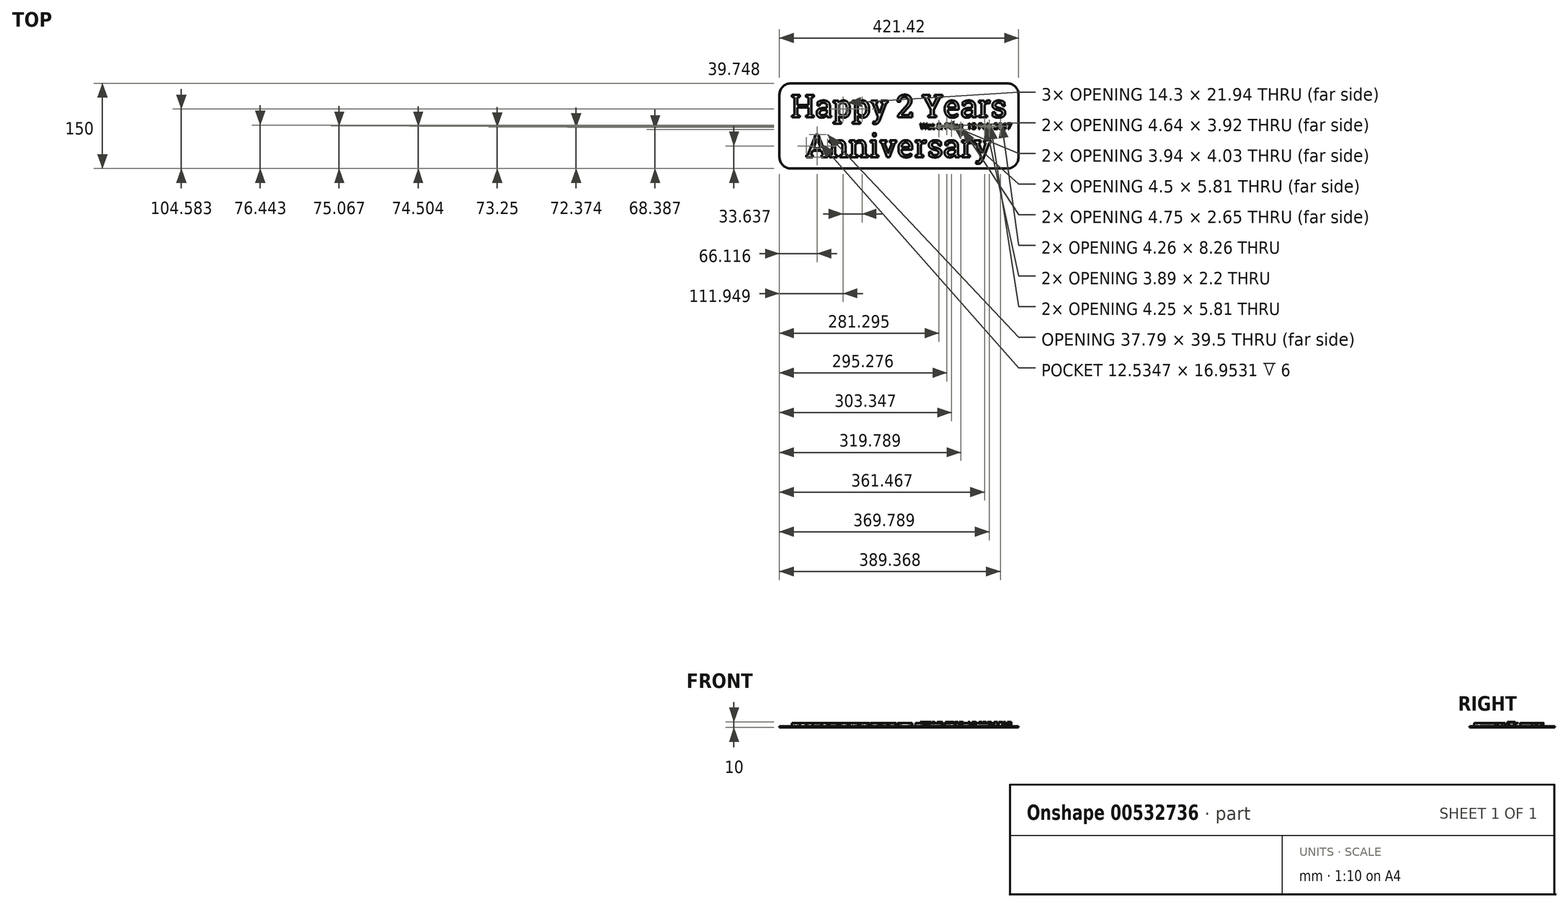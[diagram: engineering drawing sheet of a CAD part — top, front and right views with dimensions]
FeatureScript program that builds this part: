
annotation { "Feature Type Name" : "Feature", "Feature Type Description" : "" }
export const myFeature = defineFeature(function(context is Context, id is Id, definition is map)
    precondition{}
    {
        {
            var Q0;
            Q0=qCreatedBy(makeId("Top.planeOp"),FACE);
            var sketch = newSketch(context, id + "F0", { "sketchPlane" : qUnion([Q0])});
            skText(sketch, "E0", { "text": "Happy 2 Years\n", "fontName": "RobotoSlab-Regular.ttf"});
            skText(sketch, "E1", { "text": "Anniversary", "fontName": "RobotoSlab-Regular.ttf"});
            skLineSegment(sketch, "E2.bottom", {"start": v(-46.87, 27.18) * mm, "end": v(334.55, 27.18) * mm});
            skLineSegment(sketch, "E2.top", {"start": v(-46.87, -122.82) * mm, "end": v(334.55, -122.82) * mm});
            skLineSegment(sketch, "E2.left", {"start": v(-66.87, 7.18) * mm, "end": v(-66.87, -102.82) * mm});
            skLineSegment(sketch, "E2.right", {"start": v(354.55, 7.18) * mm, "end": v(354.55, -102.82) * mm});
            skPoint(sketch, "E3.visualSharp", {"position": v(354.55, 27.18) * mm});
            skArc(sketch, "E3.filletArc", {"start": v(354.55, 7.18) * mm, "mid": v(348.7, 21.32) * mm, "end": v(334.55, 27.18) * mm});
            skPoint(sketch, "E4.visualSharp", {"position": v(354.55, -122.82) * mm});
            skArc(sketch, "E4.filletArc", {"start": v(334.55, -122.82) * mm, "mid": v(348.7, -116.97) * mm, "end": v(354.55, -102.82) * mm});
            skPoint(sketch, "E5.visualSharp", {"position": v(-66.87, -122.82) * mm});
            skArc(sketch, "E5.filletArc", {"start": v(-66.87, -102.82) * mm, "mid": v(-61, -116.97) * mm, "end": v(-46.87, -122.82) * mm});
            skPoint(sketch, "E6.visualSharp", {"position": v(-66.87, 27.18) * mm});
            skArc(sketch, "E6.filletArc", {"start": v(-46.87, 27.18) * mm, "mid": v(-61, 21.32) * mm, "end": v(-66.87, 7.18) * mm});
            const initialGuessF0  = {"E0": [-0.04687, -0.03282, 1, 0, 0.04], "E1": [-0.02114, -0.10282, 1, 0, 0.04]};
            skSetInitialGuess(sketch, initialGuessF0);
            skSolve(sketch);
        }
        {
            var Q0;
            Q0=makeQuery(id+"F0.imprint","IMPRINT",FACE,{"disambiguationData":[TD([[makeQuery(id+"F0.imprint","IMPRINT",EDGE,{"derivedFrom":sQuery(id+"F0.wireOp",EDGE,"E0.sketch_text.stroke-0")}),1.0]])]});
            var sketch = newSketch(context, id + "F1", { "sketchPlane" : qUnion([Q0])});
            skText(sketch, "E7", { "text": "Wat & Pong  15 Feb 2017", "fontName": "OpenSans-Regular.ttf"});
            const initialGuessF1  = {"E7": [0.18108, -0.05328, 1, 0, 0.01]};
            skSetInitialGuess(sketch, initialGuessF1);
            skSolve(sketch);
        }
        {
            var Q0;
            Q0 = qSketchRegion(id + "F0", true);
            var Q1;
            Q1 = qSketchRegion(id + "F1", true);
            var Q2;
            Q2=makeQuery(id+"F0.imprint","IMPRINT",FACE,{"disambiguationData":[TD([[makeQuery(id+"F0.imprint","IMPRINT",EDGE,{"derivedFrom":sQuery(id+"F0.wireOp",EDGE,"E0.sketch_text.stroke-151")}),-1.0]])]});
            var Q3;
            Q3=makeQuery(id+"F0.imprint","IMPRINT",FACE,{"disambiguationData":[TD([[makeQuery(id+"F0.imprint","IMPRINT",EDGE,{"derivedFrom":sQuery(id+"F0.wireOp",EDGE,"E0.sketch_text.stroke-125")}),-1.0]])]});
            var Q4;
            Q4=makeQuery(id+"F0.imprint","IMPRINT",FACE,{"disambiguationData":[TD([[makeQuery(id+"F0.imprint","IMPRINT",EDGE,{"derivedFrom":sQuery(id+"F0.wireOp",EDGE,"E0.sketch_text.stroke-0")}),-1.0]])]});
            var Q5;
            Q5=makeQuery(id+"F0.imprint","IMPRINT",FACE,{"disambiguationData":[TD([[makeQuery(id+"F0.imprint","IMPRINT",EDGE,{"derivedFrom":sQuery(id+"F0.wireOp",EDGE,"E0.sketch_text.stroke-30")}),-1.0]])]});
            var Q6;
            Q6=makeQuery(id+"F0.imprint","IMPRINT",FACE,{"disambiguationData":[TD([[makeQuery(id+"F0.imprint","IMPRINT",EDGE,{"derivedFrom":sQuery(id+"F0.wireOp",EDGE,"E0.sketch_text.stroke-57")}),1.0]])]});
            var Q7;
            Q7=makeQuery(id+"F0.imprint","IMPRINT",FACE,{"disambiguationData":[TD([[makeQuery(id+"F0.imprint","IMPRINT",EDGE,{"derivedFrom":sQuery(id+"F0.wireOp",EDGE,"E0.sketch_text.stroke-65")}),-1.0]])]});
            var Q8;
            Q8=makeQuery(id+"F0.imprint","IMPRINT",FACE,{"disambiguationData":[TD([[makeQuery(id+"F0.imprint","IMPRINT",EDGE,{"derivedFrom":sQuery(id+"F0.wireOp",EDGE,"E0.sketch_text.stroke-85")}),1.0]])]});
            var Q9;
            Q9=makeQuery(id+"F0.imprint","IMPRINT",FACE,{"disambiguationData":[TD([[makeQuery(id+"F0.imprint","IMPRINT",EDGE,{"derivedFrom":sQuery(id+"F0.wireOp",EDGE,"E0.sketch_text.stroke-95")}),-1.0]])]});
            var Q10;
            Q10=makeQuery(id+"F1.imprint","IMPRINT",FACE,{"disambiguationData":[TD([[makeQuery(id+"F1.imprint","IMPRINT",EDGE,{"derivedFrom":makeQuery(id+"F0.imprint","IMPRINT",EDGE,{"derivedFrom":sQuery(id+"F0.wireOp",EDGE,"E0.sketch_text.stroke-95")})}),-1.0]])]});
            var Q11;
            Q11=makeQuery(id+"F0.imprint","IMPRINT",FACE,{"disambiguationData":[TD([[makeQuery(id+"F0.imprint","IMPRINT",EDGE,{"derivedFrom":sQuery(id+"F0.wireOp",EDGE,"E0.sketch_text.stroke-174")}),-1.0]])]});
            var Q12;
            Q12=makeQuery(id+"F0.imprint","IMPRINT",FACE,{"disambiguationData":[TD([[makeQuery(id+"F0.imprint","IMPRINT",EDGE,{"derivedFrom":sQuery(id+"F0.wireOp",EDGE,"E0.sketch_text.stroke-195")}),-1.0]])]});
            var Q13;
            Q13=makeQuery(id+"F0.imprint","IMPRINT",FACE,{"disambiguationData":[TD([[makeQuery(id+"F0.imprint","IMPRINT",EDGE,{"derivedFrom":sQuery(id+"F0.wireOp",EDGE,"E0.sketch_text.stroke-212")}),1.0]])]});
            var Q14;
            Q14=makeQuery(id+"F0.imprint","IMPRINT",FACE,{"disambiguationData":[TD([[makeQuery(id+"F0.imprint","IMPRINT",EDGE,{"derivedFrom":sQuery(id+"F0.wireOp",EDGE,"E0.sketch_text.stroke-246")}),1.0]])]});
            var Q15;
            Q15=makeQuery(id+"F0.imprint","IMPRINT",FACE,{"disambiguationData":[TD([[makeQuery(id+"F0.imprint","IMPRINT",EDGE,{"derivedFrom":sQuery(id+"F0.wireOp",EDGE,"E0.sketch_text.stroke-219")}),-1.0]])]});
            var Q16;
            Q16=makeQuery(id+"F0.imprint","IMPRINT",FACE,{"disambiguationData":[TD([[makeQuery(id+"F0.imprint","IMPRINT",EDGE,{"derivedFrom":sQuery(id+"F0.wireOp",EDGE,"E0.sketch_text.stroke-254")}),-1.0]])]});
            var Q17;
            Q17=makeQuery(id+"F0.imprint","IMPRINT",FACE,{"disambiguationData":[TD([[makeQuery(id+"F0.imprint","IMPRINT",EDGE,{"derivedFrom":sQuery(id+"F0.wireOp",EDGE,"E0.sketch_text.stroke-273")}),-1.0]])]});
            var Q18;
            Q18=makeQuery(id+"F0.imprint","IMPRINT",FACE,{"disambiguationData":[TD([[makeQuery(id+"F0.imprint","IMPRINT",EDGE,{"derivedFrom":sQuery(id+"F0.wireOp",EDGE,"E1.sketch_text.stroke-231")}),-1.0]])]});
            var Q19;
            Q19=makeQuery(id+"F0.imprint","IMPRINT",FACE,{"disambiguationData":[TD([[makeQuery(id+"F0.imprint","IMPRINT",EDGE,{"derivedFrom":sQuery(id+"F0.wireOp",EDGE,"E1.sketch_text.stroke-212")}),-1.0]])]});
            var Q20;
            Q20=makeQuery(id+"F0.imprint","IMPRINT",FACE,{"disambiguationData":[TD([[makeQuery(id+"F0.imprint","IMPRINT",EDGE,{"derivedFrom":sQuery(id+"F0.wireOp",EDGE,"E1.sketch_text.stroke-177")}),-1.0]])]});
            var Q21;
            Q21=makeQuery(id+"F0.imprint","IMPRINT",FACE,{"disambiguationData":[TD([[makeQuery(id+"F0.imprint","IMPRINT",EDGE,{"derivedFrom":sQuery(id+"F0.wireOp",EDGE,"E1.sketch_text.stroke-204")}),1.0]])]});
            var Q22;
            Q22=makeQuery(id+"F0.imprint","IMPRINT",FACE,{"disambiguationData":[TD([[makeQuery(id+"F0.imprint","IMPRINT",EDGE,{"derivedFrom":sQuery(id+"F0.wireOp",EDGE,"E1.sketch_text.stroke-147")}),-1.0]])]});
            var Q23;
            Q23=makeQuery(id+"F0.imprint","IMPRINT",FACE,{"disambiguationData":[TD([[makeQuery(id+"F0.imprint","IMPRINT",EDGE,{"derivedFrom":sQuery(id+"F0.wireOp",EDGE,"E1.sketch_text.stroke-128")}),-1.0]])]});
            var Q24;
            Q24=makeQuery(id+"F0.imprint","IMPRINT",FACE,{"disambiguationData":[TD([[makeQuery(id+"F0.imprint","IMPRINT",EDGE,{"derivedFrom":sQuery(id+"F0.wireOp",EDGE,"E1.sketch_text.stroke-86")}),-1.0]])]});
            var Q25;
            Q25=makeQuery(id+"F0.imprint","IMPRINT",FACE,{"disambiguationData":[TD([[makeQuery(id+"F0.imprint","IMPRINT",EDGE,{"derivedFrom":sQuery(id+"F0.wireOp",EDGE,"E1.sketch_text.stroke-72")}),-1.0]])]});
            var Q26;
            Q26=makeQuery(id+"F0.imprint","IMPRINT",FACE,{"disambiguationData":[TD([[makeQuery(id+"F0.imprint","IMPRINT",EDGE,{"derivedFrom":sQuery(id+"F0.wireOp",EDGE,"E1.sketch_text.stroke-82")}),-1.0]])]});
            var Q27;
            Q27=makeQuery(id+"F0.imprint","IMPRINT",FACE,{"disambiguationData":[TD([[makeQuery(id+"F0.imprint","IMPRINT",EDGE,{"derivedFrom":sQuery(id+"F0.wireOp",EDGE,"E1.sketch_text.stroke-46")}),-1.0]])]});
            var Q28;
            Q28=makeQuery(id+"F0.imprint","IMPRINT",FACE,{"disambiguationData":[TD([[makeQuery(id+"F0.imprint","IMPRINT",EDGE,{"derivedFrom":sQuery(id+"F0.wireOp",EDGE,"E1.sketch_text.stroke-104")}),-1.0]])]});
            var Q29;
            Q29=makeQuery(id+"F0.imprint","IMPRINT",FACE,{"disambiguationData":[TD([[makeQuery(id+"F0.imprint","IMPRINT",EDGE,{"derivedFrom":sQuery(id+"F0.wireOp",EDGE,"E1.sketch_text.stroke-121")}),1.0]])]});
            var Q30;
            Q30=makeQuery(id+"F0.imprint","IMPRINT",FACE,{"disambiguationData":[TD([[makeQuery(id+"F0.imprint","IMPRINT",EDGE,{"derivedFrom":sQuery(id+"F0.wireOp",EDGE,"E1.sketch_text.stroke-20")}),-1.0]])]});
            var Q31;
            Q31=makeQuery(id+"F1.imprint","IMPRINT",FACE,{"disambiguationData":[TD([[makeQuery(id+"F1.imprint","IMPRINT",EDGE,{"derivedFrom":makeQuery(id+"F0.imprint","IMPRINT",EDGE,{"derivedFrom":sQuery(id+"F0.wireOp",EDGE,"E1.sketch_text.stroke-0")})}),-1.0]])]});
            var Q32;
            Q32=makeQuery(id+"F0.imprint","IMPRINT",FACE,{"disambiguationData":[TD([[makeQuery(id+"F0.imprint","IMPRINT",EDGE,{"derivedFrom":sQuery(id+"F0.wireOp",EDGE,"E1.sketch_text.stroke-16")}),1.0]])]});
            extrude(context, id + "F2", {"entities" : qUnion([Q0, Q1, Q2, Q3, Q4, Q5, Q6, Q7, Q8, Q9, Q10, Q11, Q12, Q13, Q14, Q15, Q16, Q17, Q18, Q19, Q20, Q21, Q22, Q23, Q24, Q25, Q26, Q27, Q28, Q29, Q30, Q31, Q32]), "depth" : 2 * mm, "offsetDistance" : 25 * mm});
        }
        {
            var Q0;
            Q0=makeQuery(id+"F1.imprint","IMPRINT",FACE,{"disambiguationData":[TD([[makeQuery(id+"F1.imprint","IMPRINT",EDGE,{"derivedFrom":makeQuery(id+"F0.imprint","IMPRINT",EDGE,{"derivedFrom":sQuery(id+"F0.wireOp",EDGE,"E0.sketch_text.stroke-30")})}),-1.0]])]});
            var Q1;
            Q1=makeQuery(id+"F1.imprint","IMPRINT",FACE,{"disambiguationData":[TD([[makeQuery(id+"F1.imprint","IMPRINT",EDGE,{"derivedFrom":makeQuery(id+"F0.imprint","IMPRINT",EDGE,{"derivedFrom":sQuery(id+"F0.wireOp",EDGE,"E0.sketch_text.stroke-219")})}),-1.0]])]});
            var Q2;
            Q2=makeQuery(id+"F1.imprint","IMPRINT",FACE,{"disambiguationData":[TD([[makeQuery(id+"F1.imprint","IMPRINT",EDGE,{"derivedFrom":makeQuery(id+"F0.imprint","IMPRINT",EDGE,{"derivedFrom":sQuery(id+"F0.wireOp",EDGE,"E1.sketch_text.stroke-0")})}),-1.0]])]});
            var Q3;
            Q3=makeQuery(id+"F0.imprint","IMPRINT",FACE,{"disambiguationData":[TD([[makeQuery(id+"F0.imprint","IMPRINT",EDGE,{"derivedFrom":sQuery(id+"F0.wireOp",EDGE,"E1.sketch_text.stroke-72")}),-1.0]])]});
            var Q4;
            Q4=makeQuery(id+"F1.imprint","IMPRINT",FACE,{"disambiguationData":[TD([[makeQuery(id+"F1.imprint","IMPRINT",EDGE,{"derivedFrom":makeQuery(id+"F0.imprint","IMPRINT",EDGE,{"derivedFrom":sQuery(id+"F0.wireOp",EDGE,"E1.sketch_text.stroke-82")})}),-1.0]])]});
            var Q5;
            Q5=makeQuery(id+"F0.imprint","IMPRINT",FACE,{"disambiguationData":[TD([[makeQuery(id+"F0.imprint","IMPRINT",EDGE,{"derivedFrom":sQuery(id+"F0.wireOp",EDGE,"E1.sketch_text.stroke-86")}),-1.0]])]});
            var Q6;
            Q6=makeQuery(id+"F1.imprint","IMPRINT",FACE,{"disambiguationData":[TD([[makeQuery(id+"F1.imprint","IMPRINT",EDGE,{"derivedFrom":makeQuery(id+"F0.imprint","IMPRINT",EDGE,{"derivedFrom":sQuery(id+"F0.wireOp",EDGE,"E1.sketch_text.stroke-104")})}),-1.0]])]});
            var Q7;
            Q7=makeQuery(id+"F0.imprint","IMPRINT",FACE,{"disambiguationData":[TD([[makeQuery(id+"F0.imprint","IMPRINT",EDGE,{"derivedFrom":sQuery(id+"F0.wireOp",EDGE,"E1.sketch_text.stroke-128")}),-1.0]])]});
            var Q8;
            Q8=makeQuery(id+"F0.imprint","IMPRINT",FACE,{"disambiguationData":[TD([[makeQuery(id+"F0.imprint","IMPRINT",EDGE,{"derivedFrom":sQuery(id+"F0.wireOp",EDGE,"E1.sketch_text.stroke-147")}),-1.0]])]});
            var Q9;
            Q9=makeQuery(id+"F1.imprint","IMPRINT",FACE,{"disambiguationData":[TD([[makeQuery(id+"F1.imprint","IMPRINT",EDGE,{"derivedFrom":makeQuery(id+"F0.imprint","IMPRINT",EDGE,{"derivedFrom":sQuery(id+"F0.wireOp",EDGE,"E1.sketch_text.stroke-177")})}),-1.0]])]});
            var Q10;
            Q10=makeQuery(id+"F0.imprint","IMPRINT",FACE,{"disambiguationData":[TD([[makeQuery(id+"F0.imprint","IMPRINT",EDGE,{"derivedFrom":sQuery(id+"F0.wireOp",EDGE,"E1.sketch_text.stroke-20")}),-1.0]])]});
            var Q11;
            Q11=makeQuery(id+"F0.imprint","IMPRINT",FACE,{"disambiguationData":[TD([[makeQuery(id+"F0.imprint","IMPRINT",EDGE,{"derivedFrom":sQuery(id+"F0.wireOp",EDGE,"E1.sketch_text.stroke-46")}),-1.0]])]});
            var Q12;
            Q12=makeQuery(id+"F0.imprint","IMPRINT",FACE,{"disambiguationData":[TD([[makeQuery(id+"F0.imprint","IMPRINT",EDGE,{"derivedFrom":sQuery(id+"F0.wireOp",EDGE,"E1.sketch_text.stroke-212")}),-1.0]])]});
            var Q13;
            Q13=makeQuery(id+"F0.imprint","IMPRINT",FACE,{"disambiguationData":[TD([[makeQuery(id+"F0.imprint","IMPRINT",EDGE,{"derivedFrom":sQuery(id+"F0.wireOp",EDGE,"E1.sketch_text.stroke-231")}),-1.0]])]});
            var Q14;
            Q14=makeQuery(id+"F0.imprint","IMPRINT",FACE,{"disambiguationData":[TD([[makeQuery(id+"F0.imprint","IMPRINT",EDGE,{"derivedFrom":sQuery(id+"F0.wireOp",EDGE,"E0.sketch_text.stroke-0")}),-1.0]])]});
            var Q15;
            Q15=makeQuery(id+"F0.imprint","IMPRINT",FACE,{"disambiguationData":[TD([[makeQuery(id+"F0.imprint","IMPRINT",EDGE,{"derivedFrom":sQuery(id+"F0.wireOp",EDGE,"E0.sketch_text.stroke-65")}),-1.0]])]});
            var Q16;
            Q16=makeQuery(id+"F0.imprint","IMPRINT",FACE,{"disambiguationData":[TD([[makeQuery(id+"F0.imprint","IMPRINT",EDGE,{"derivedFrom":sQuery(id+"F0.wireOp",EDGE,"E0.sketch_text.stroke-95")}),-1.0]])]});
            var Q17;
            Q17=makeQuery(id+"F0.imprint","IMPRINT",FACE,{"disambiguationData":[TD([[makeQuery(id+"F0.imprint","IMPRINT",EDGE,{"derivedFrom":sQuery(id+"F0.wireOp",EDGE,"E0.sketch_text.stroke-125")}),-1.0]])]});
            var Q18;
            Q18=makeQuery(id+"F0.imprint","IMPRINT",FACE,{"disambiguationData":[TD([[makeQuery(id+"F0.imprint","IMPRINT",EDGE,{"derivedFrom":sQuery(id+"F0.wireOp",EDGE,"E0.sketch_text.stroke-151")}),-1.0]])]});
            var Q19;
            Q19=makeQuery(id+"F0.imprint","IMPRINT",FACE,{"disambiguationData":[TD([[makeQuery(id+"F0.imprint","IMPRINT",EDGE,{"derivedFrom":sQuery(id+"F0.wireOp",EDGE,"E0.sketch_text.stroke-174")}),-1.0]])]});
            var Q20;
            Q20=makeQuery(id+"F0.imprint","IMPRINT",FACE,{"disambiguationData":[TD([[makeQuery(id+"F0.imprint","IMPRINT",EDGE,{"derivedFrom":sQuery(id+"F0.wireOp",EDGE,"E0.sketch_text.stroke-195")}),-1.0]])]});
            var Q21;
            Q21=makeQuery(id+"F0.imprint","IMPRINT",FACE,{"disambiguationData":[TD([[makeQuery(id+"F0.imprint","IMPRINT",EDGE,{"derivedFrom":sQuery(id+"F0.wireOp",EDGE,"E1.sketch_text.stroke-16")}),1.0]])]});
            var Q22;
            Q22=makeQuery(id+"F0.imprint","IMPRINT",FACE,{"disambiguationData":[TD([[makeQuery(id+"F0.imprint","IMPRINT",EDGE,{"derivedFrom":sQuery(id+"F0.wireOp",EDGE,"E0.sketch_text.stroke-254")}),-1.0]])]});
            var Q23;
            Q23=makeQuery(id+"F0.imprint","IMPRINT",FACE,{"disambiguationData":[TD([[makeQuery(id+"F0.imprint","IMPRINT",EDGE,{"derivedFrom":sQuery(id+"F0.wireOp",EDGE,"E0.sketch_text.stroke-273")}),-1.0]])]});
            var Q24;
            Q24=makeQuery(id+"F0.imprint","IMPRINT",FACE,{"disambiguationData":[TD([[makeQuery(id+"F0.imprint","IMPRINT",EDGE,{"derivedFrom":sQuery(id+"F0.wireOp",EDGE,"E0.sketch_text.stroke-57")}),1.0]])]});
            var Q25;
            Q25=makeQuery(id+"F0.imprint","IMPRINT",FACE,{"disambiguationData":[TD([[makeQuery(id+"F0.imprint","IMPRINT",EDGE,{"derivedFrom":sQuery(id+"F0.wireOp",EDGE,"E1.sketch_text.stroke-121")}),1.0]])]});
            var Q26;
            Q26=makeQuery(id+"F0.imprint","IMPRINT",FACE,{"disambiguationData":[TD([[makeQuery(id+"F0.imprint","IMPRINT",EDGE,{"derivedFrom":sQuery(id+"F0.wireOp",EDGE,"E1.sketch_text.stroke-204")}),1.0]])]});
            extrude(context, id + "F3", {"entities" : qUnion([Q0, Q1, Q2, Q3, Q4, Q5, Q6, Q7, Q8, Q9, Q10, Q11, Q12, Q13, Q14, Q15, Q16, Q17, Q18, Q19, Q20, Q21, Q22, Q23, Q24, Q25, Q26]), "depth" : 8 * mm, "offsetDistance" : 25 * mm});
        }
        {
            var Q0;
            Q0=makeQuery(id+"F0.imprint","IMPRINT",FACE,{"disambiguationData":[TD([[makeQuery(id+"F0.imprint","IMPRINT",EDGE,{"derivedFrom":sQuery(id+"F0.wireOp",EDGE,"E0.sketch_text.stroke-57")}),1.0]])]});
            var Q1;
            Q1=makeQuery(id+"F0.imprint","IMPRINT",FACE,{"disambiguationData":[TD([[makeQuery(id+"F0.imprint","IMPRINT",EDGE,{"derivedFrom":sQuery(id+"F0.wireOp",EDGE,"E0.sketch_text.stroke-212")}),1.0]])]});
            var Q2;
            Q2=makeQuery(id+"F0.imprint","IMPRINT",FACE,{"disambiguationData":[TD([[makeQuery(id+"F0.imprint","IMPRINT",EDGE,{"derivedFrom":sQuery(id+"F0.wireOp",EDGE,"E0.sketch_text.stroke-246")}),1.0]])]});
            var Q3;
            Q3=makeQuery(id+"F0.imprint","IMPRINT",FACE,{"disambiguationData":[TD([[makeQuery(id+"F0.imprint","IMPRINT",EDGE,{"derivedFrom":sQuery(id+"F0.wireOp",EDGE,"E1.sketch_text.stroke-16")}),1.0]])]});
            var Q4;
            Q4=makeQuery(id+"F0.imprint","IMPRINT",FACE,{"disambiguationData":[TD([[makeQuery(id+"F0.imprint","IMPRINT",EDGE,{"derivedFrom":sQuery(id+"F0.wireOp",EDGE,"E1.sketch_text.stroke-121")}),1.0]])]});
            var Q5;
            Q5=makeQuery(id+"F0.imprint","IMPRINT",FACE,{"disambiguationData":[TD([[makeQuery(id+"F0.imprint","IMPRINT",EDGE,{"derivedFrom":sQuery(id+"F0.wireOp",EDGE,"E1.sketch_text.stroke-204")}),1.0]])]});
            extrude(context, id + "F4", {"entities" : qUnion([Q0, Q1, Q2, Q3, Q4, Q5]), "operationType" : NewBodyOperationType.REMOVE, "oppositeDirection" : true, "depth" : 25 * mm, "offsetDistance" : 25 * mm, "hasSecondDirection" : true, "secondDirectionOppositeDirection" : false, "secondDirectionDepth" : 25 * mm});
        }
        {
            var Q0;
            Q0=makeQuery(id+"F0.imprint","IMPRINT",FACE,{"disambiguationData":[TD([[makeQuery(id+"F0.imprint","IMPRINT",EDGE,{"derivedFrom":sQuery(id+"F0.wireOp",EDGE,"E0.sketch_text.stroke-57")}),1.0]])]});
            var Q1;
            Q1=makeQuery(id+"F0.imprint","IMPRINT",FACE,{"disambiguationData":[TD([[makeQuery(id+"F0.imprint","IMPRINT",EDGE,{"derivedFrom":sQuery(id+"F0.wireOp",EDGE,"E1.sketch_text.stroke-16")}),1.0]])]});
            var Q2;
            Q2=makeQuery(id+"F0.imprint","IMPRINT",FACE,{"disambiguationData":[TD([[makeQuery(id+"F0.imprint","IMPRINT",EDGE,{"derivedFrom":sQuery(id+"F0.wireOp",EDGE,"E0.sketch_text.stroke-212")}),1.0]])]});
            var Q3;
            Q3=makeQuery(id+"F0.imprint","IMPRINT",FACE,{"disambiguationData":[TD([[makeQuery(id+"F0.imprint","IMPRINT",EDGE,{"derivedFrom":sQuery(id+"F0.wireOp",EDGE,"E0.sketch_text.stroke-246")}),1.0]])]});
            var Q4;
            Q4=makeQuery(id+"F0.imprint","IMPRINT",FACE,{"disambiguationData":[TD([[makeQuery(id+"F0.imprint","IMPRINT",EDGE,{"derivedFrom":sQuery(id+"F0.wireOp",EDGE,"E1.sketch_text.stroke-204")}),1.0]])]});
            var Q5;
            Q5=makeQuery(id+"F0.imprint","IMPRINT",FACE,{"disambiguationData":[TD([[makeQuery(id+"F0.imprint","IMPRINT",EDGE,{"derivedFrom":sQuery(id+"F0.wireOp",EDGE,"E1.sketch_text.stroke-121")}),1.0]])]});
            extrude(context, id + "F5", {"entities" : qUnion([Q0, Q1, Q2, Q3, Q4, Q5]), "operationType" : NewBodyOperationType.ADD, "depth" : 2 * mm, "offsetDistance" : 25 * mm});
        }
        {
            var Q0;
            Q0 = qSketchRegion(id + "F1", true);
            extrude(context, id + "F6", {"entities" : qUnion([Q0]), "depth" : 10 * mm, "offsetDistance" : 25 * mm});
        }
    });
